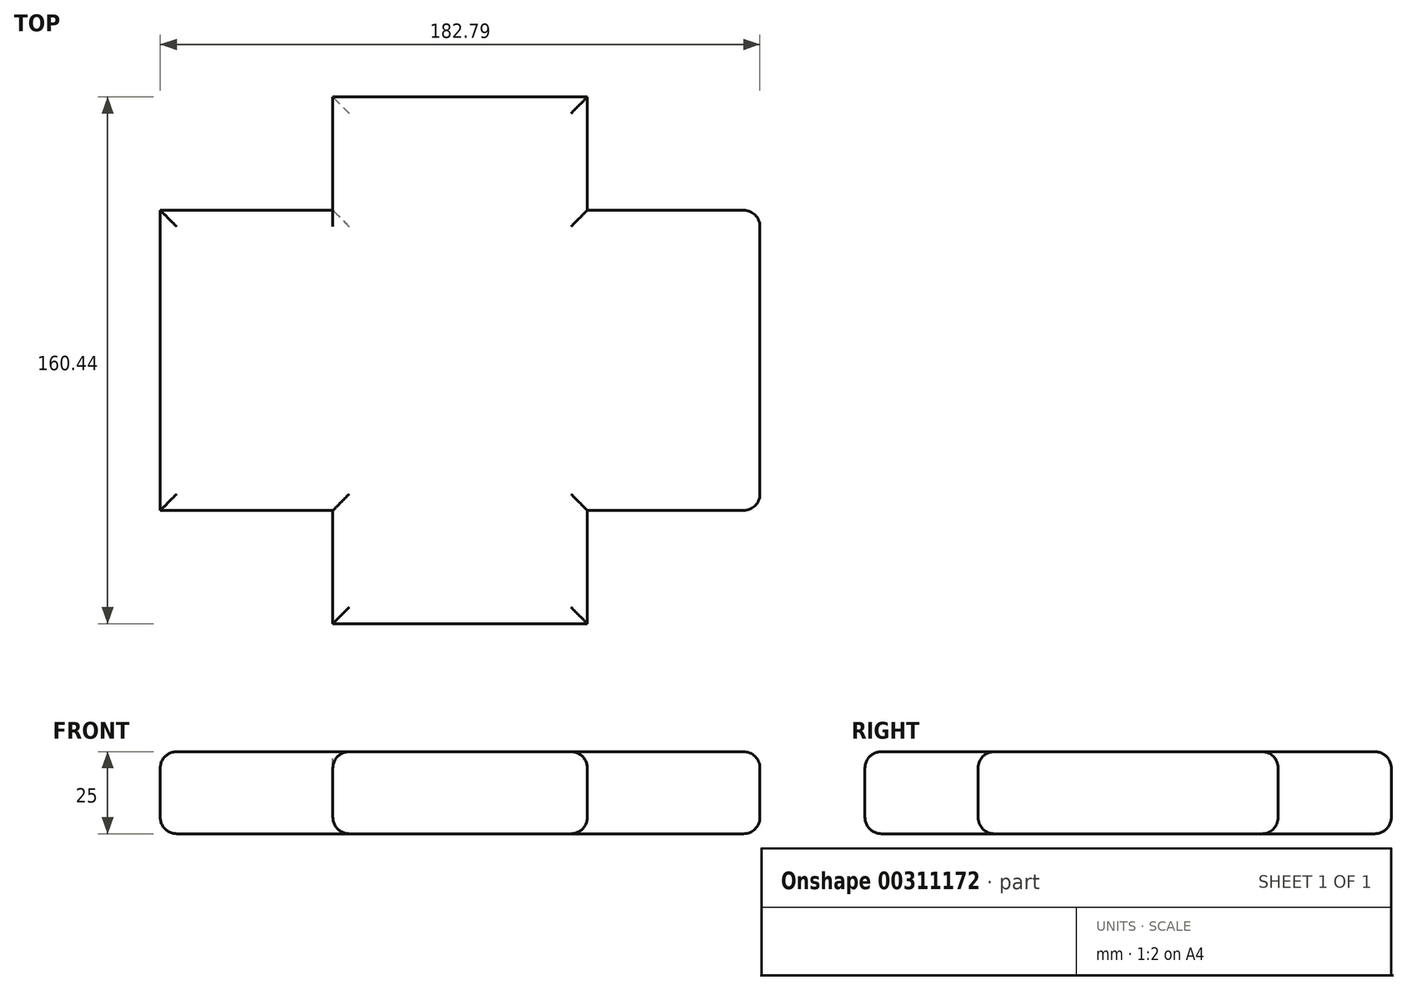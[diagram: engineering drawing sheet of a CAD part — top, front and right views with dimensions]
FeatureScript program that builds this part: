
annotation { "Feature Type Name" : "Feature", "Feature Type Description" : "" }
export const myFeature = defineFeature(function(context is Context, id is Id, definition is map)
    precondition{}
    {
        {
            var Q0;
            Q0=qCreatedBy(makeId("Top.planeOp"),FACE);
            var sketch = newSketch(context, id + "F0", { "sketchPlane" : qUnion([Q0])});
            skLineSegment(sketch, "E0.bottom", {"start": v(-12.81, -23.97) * mm, "end": v(-195.6, -23.97) * mm});
            skLineSegment(sketch, "E0.top", {"start": v(-12.81, 67.5) * mm, "end": v(-195.6, 67.5) * mm});
            skLineSegment(sketch, "E0.left", {"start": v(-12.81, -23.97) * mm, "end": v(-12.81, 67.5) * mm});
            skLineSegment(sketch, "E0.right", {"start": v(-195.6, -23.97) * mm, "end": v(-195.6, 67.5) * mm});
            skPoint(sketch, "E0.middle", {"position": v(-104.2, 21.77) * mm});
            skLineSegment(sketch, "E1.bottom", {"start": v(-143, 101.99) * mm, "end": v(-65.42, 101.99) * mm});
            skLineSegment(sketch, "E1.top", {"start": v(-143, -58.45) * mm, "end": v(-65.42, -58.45) * mm});
            skLineSegment(sketch, "E1.left", {"start": v(-143, 101.99) * mm, "end": v(-143, -58.45) * mm});
            skLineSegment(sketch, "E1.right", {"start": v(-65.42, 101.99) * mm, "end": v(-65.42, -58.45) * mm});
            skSolve(sketch);
        }
        {
            var Q0;
            {var subQ5=sQuery(id+"F0.wireOp",EDGE,"E1.top");Q0=makeQuery(id+"F0.imprint","IMPRINT",FACE,{"disambiguationData":[TD([[makeQuery(id+"F0.imprint","IMPRINT",EDGE,{"derivedFrom":subQ5}),1.0]])]});}
            var Q1;
            {var subQ5=sQuery(id+"F0.wireOp",EDGE,"E1.bottom");Q1=makeQuery(id+"F0.imprint","IMPRINT",FACE,{"disambiguationData":[TD([[makeQuery(id+"F0.imprint","IMPRINT",EDGE,{"derivedFrom":subQ5}),-1.0]])]});}
            var Q2;
            {var subQ0=sQuery(id+"F0.wireOp",EDGE,"E1.right");var subQ1=sQuery(id+"F0.wireOp",EDGE,"E0.bottom");var subQ2=makeQuery(id+"F0.imprint","INTERSECT",VERTEX,{"derivedFrom":[subQ1,subQ0]});Q2=makeQuery(id+"F0.imprint","IMPRINT",FACE,{"disambiguationData":[TD([[makeQuery(id+"F0.imprint","IMPRINT",EDGE,{"disambiguationData":[TD([[subQ2,-1.0]])],"derivedFrom":subQ1}),-1.0]])]});}
            var Q3;
            {var subQ0=sQuery(id+"F0.wireOp",EDGE,"E0.right");Q3=makeQuery(id+"F0.imprint","IMPRINT",FACE,{"disambiguationData":[TD([[makeQuery(id+"F0.imprint","IMPRINT",EDGE,{"derivedFrom":subQ0}),-1.0]])]});}
            var Q4;
            {var subQ0=sQuery(id+"F0.wireOp",EDGE,"E0.left");Q4=makeQuery(id+"F0.imprint","IMPRINT",FACE,{"disambiguationData":[TD([[makeQuery(id+"F0.imprint","IMPRINT",EDGE,{"derivedFrom":subQ0}),1.0]])]});}
            extrude(context, id + "F1", {"entities" : qUnion([Q0, Q1, Q2, Q3, Q4]), "depth" : 25 * mm});
        }
        {
            var Q0;
            Q0=makeQuery(id+"F1.opExtrude","SWEPT_FACE",FACE,{"disambiguationData":[OSD([sQuery(id+"F0.wireOp",EDGE,"E0.left")])]});
            var Q1;
            Q1=makeQuery(id+"F1.opExtrude","CAP_FACE",FACE,{"disambiguationData":[OSD([sQuery(id+"F0.wireOp",EDGE,"E0.bottom"),sQuery(id+"F0.wireOp",EDGE,"E0.top"),sQuery(id+"F0.wireOp",EDGE,"E0.left"),sQuery(id+"F0.wireOp",EDGE,"E0.right"),sQuery(id+"F0.wireOp",EDGE,"E1.bottom"),sQuery(id+"F0.wireOp",EDGE,"E1.top"),sQuery(id+"F0.wireOp",EDGE,"E1.left"),sQuery(id+"F0.wireOp",EDGE,"E1.right")])],"isStart":true});
            var Q2;
            Q2=makeQuery(id+"F1.opExtrude","CAP_EDGE",EDGE,{"disambiguationData":[OSD([sQuery(id+"F0.wireOp",EDGE,"E1.top")])],"isStart":false});
            var Q3;
            {var subQ0=sQuery(id+"F0.wireOp",EDGE,"E1.left");Q3=makeQuery(id+"F1.opExtrude","CAP_EDGE",EDGE,{"disambiguationData":[OSD([subQ0]),TDD([makeQuery(id+"F0.imprint","IMPRINT",EDGE,{"disambiguationData":[TD([[makeQuery(id+"F0.imprint","INTERSECT",VERTEX,{"derivedFrom":[sQuery(id+"F0.wireOp",EDGE,"E1.top"),subQ0]}),1.0]])],"derivedFrom":subQ0})])],"isStart":false});}
            var Q4;
            {var subQ0=sQuery(id+"F0.wireOp",EDGE,"E0.bottom");Q4=makeQuery(id+"F1.opExtrude","CAP_EDGE",EDGE,{"disambiguationData":[OSD([subQ0]),TDD([makeQuery(id+"F0.imprint","IMPRINT",EDGE,{"disambiguationData":[TD([[makeQuery(id+"F0.imprint","INTERSECT",VERTEX,{"derivedFrom":[subQ0,sQuery(id+"F0.wireOp",EDGE,"E0.right")]}),1.0]])],"derivedFrom":subQ0})])],"isStart":false});}
            var Q5;
            Q5=makeQuery(id+"F1.opExtrude","CAP_EDGE",EDGE,{"disambiguationData":[OSD([sQuery(id+"F0.wireOp",EDGE,"E0.right")])],"isStart":false});
            var Q6;
            {var subQ0=sQuery(id+"F0.wireOp",EDGE,"E0.top");Q6=makeQuery(id+"F1.opExtrude","CAP_EDGE",EDGE,{"disambiguationData":[OSD([subQ0]),TDD([makeQuery(id+"F0.imprint","IMPRINT",EDGE,{"disambiguationData":[TD([[makeQuery(id+"F0.imprint","INTERSECT",VERTEX,{"derivedFrom":[subQ0,sQuery(id+"F0.wireOp",EDGE,"E0.right")]}),1.0]])],"derivedFrom":subQ0})])],"isStart":false});}
            var Q7;
            Q7=makeQuery(id+"F1.opExtrude","CAP_EDGE",EDGE,{"disambiguationData":[OSD([sQuery(id+"F0.wireOp",EDGE,"E1.bottom")])],"isStart":false});
            var Q8;
            {var subQ0=sQuery(id+"F0.wireOp",EDGE,"E1.right");Q8=makeQuery(id+"F1.opExtrude","CAP_EDGE",EDGE,{"disambiguationData":[OSD([subQ0]),TDD([makeQuery(id+"F0.imprint","IMPRINT",EDGE,{"disambiguationData":[TD([[makeQuery(id+"F0.imprint","INTERSECT",VERTEX,{"derivedFrom":[sQuery(id+"F0.wireOp",EDGE,"E1.bottom"),subQ0]}),-1.0]])],"derivedFrom":subQ0})])],"isStart":false});}
            var Q9;
            {var subQ0=sQuery(id+"F0.wireOp",EDGE,"E0.top");Q9=makeQuery(id+"F1.opExtrude","CAP_EDGE",EDGE,{"disambiguationData":[OSD([subQ0]),TDD([makeQuery(id+"F0.imprint","IMPRINT",EDGE,{"disambiguationData":[TD([[makeQuery(id+"F0.imprint","INTERSECT",VERTEX,{"derivedFrom":[subQ0,sQuery(id+"F0.wireOp",EDGE,"E0.left")]}),-1.0]])],"derivedFrom":subQ0})])],"isStart":false});}
            var Q10;
            {var subQ0=sQuery(id+"F0.wireOp",EDGE,"E0.bottom");Q10=makeQuery(id+"F1.opExtrude","CAP_EDGE",EDGE,{"disambiguationData":[OSD([subQ0]),TDD([makeQuery(id+"F0.imprint","IMPRINT",EDGE,{"disambiguationData":[TD([[makeQuery(id+"F0.imprint","INTERSECT",VERTEX,{"derivedFrom":[subQ0,sQuery(id+"F0.wireOp",EDGE,"E0.left")]}),-1.0]])],"derivedFrom":subQ0})])],"isStart":false});}
            var Q11;
            {var subQ0=sQuery(id+"F0.wireOp",EDGE,"E1.right");Q11=makeQuery(id+"F1.opExtrude","CAP_EDGE",EDGE,{"disambiguationData":[OSD([subQ0]),TDD([makeQuery(id+"F0.imprint","IMPRINT",EDGE,{"disambiguationData":[TD([[makeQuery(id+"F0.imprint","INTERSECT",VERTEX,{"derivedFrom":[sQuery(id+"F0.wireOp",EDGE,"E1.top"),subQ0]}),1.0]])],"derivedFrom":subQ0})])],"isStart":false});}
            fillet(context, id + "F2", {"entities" : qUnion([Q0, Q1, Q2, Q3, Q4, Q5, Q6, Q7, Q8, Q9, Q10, Q11]), "radius" : 5 * mm, "tangentPropagation" : true, "allowEdgeOverflow" : false});
        }
    });
